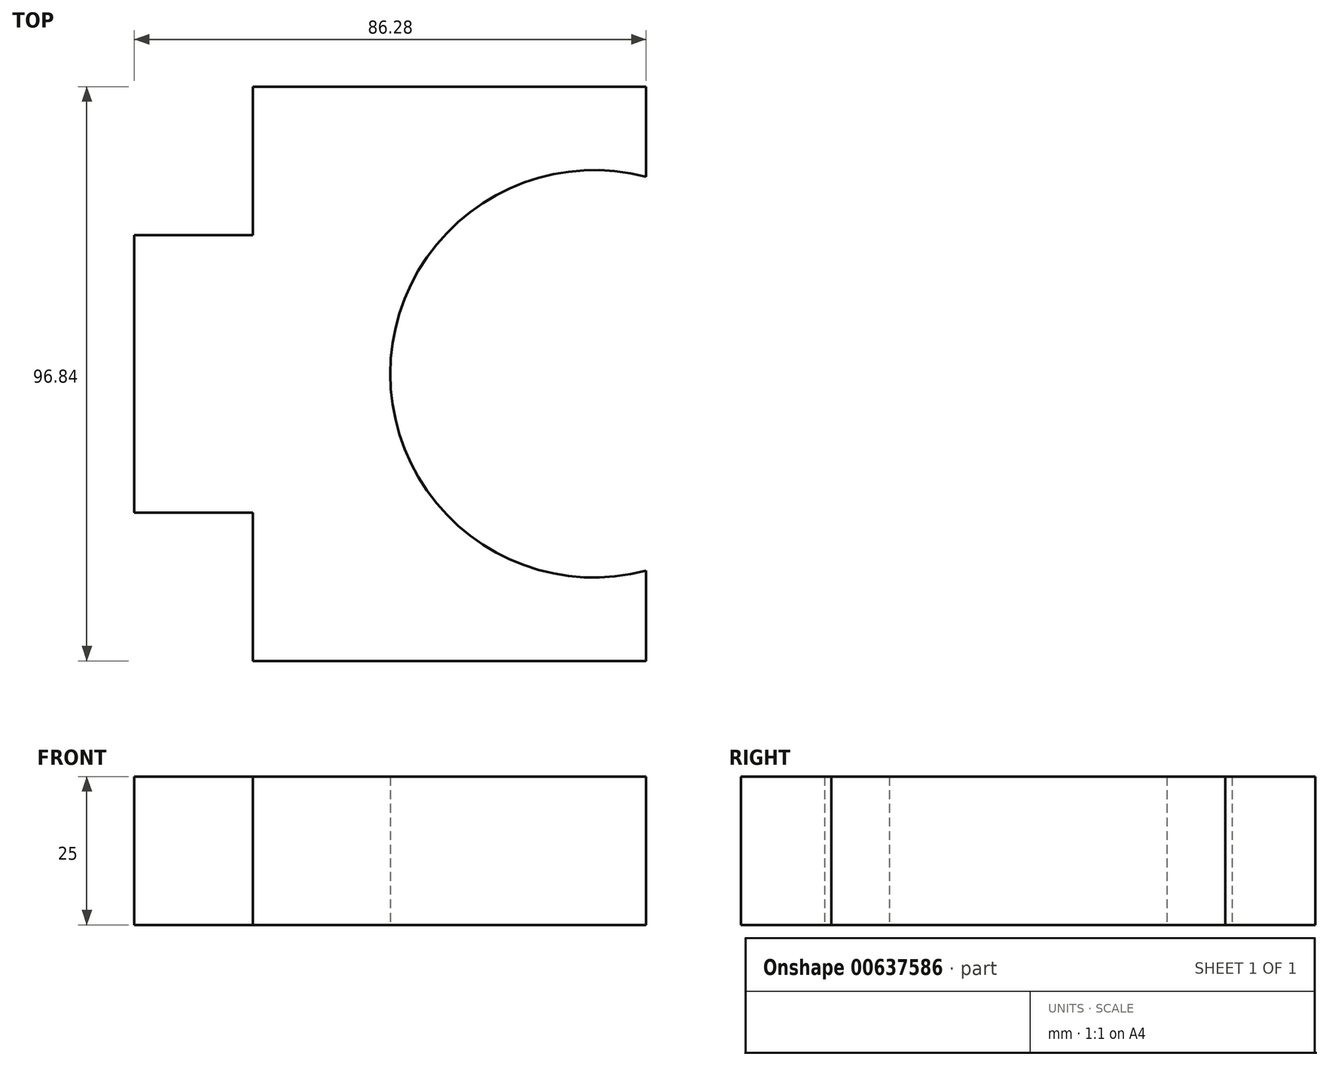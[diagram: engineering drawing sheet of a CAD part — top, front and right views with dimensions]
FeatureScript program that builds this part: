
annotation { "Feature Type Name" : "Feature", "Feature Type Description" : "" }
export const myFeature = defineFeature(function(context is Context, id is Id, definition is map)
    precondition{}
    {
        {
            var Q0;
            Q0=qCreatedBy(makeId("Top.planeOp"),FACE);
            var sketch = newSketch(context, id + "F0", { "sketchPlane" : qUnion([Q0])});
            skLineSegment(sketch, "E0", {"start": v(32.1, 48.42) * mm, "end": v(32.1, 33.2) * mm});
            skArc(sketch, "E1", {"start": v(32.1, 33.2) * mm, "mid": v(-11.04, 0) * mm, "end": v(32.1, -33.2) * mm});
            skLineSegment(sketch, "E2.trimOffspring", {"start": v(32.1, -33.2) * mm, "end": v(32.1, -48.42) * mm});
            skLineSegment(sketch, "E3", {"start": v(32.1, 48.42) * mm, "end": v(-34.2, 48.42) * mm});
            skPoint(sketch, "E4.end.orphan", {"position": v(-34.2, 21.15) * mm});
            skPoint(sketch, "E5.start.orphan", {"position": v(-34.2, -52.39) * mm});
            skLineSegment(sketch, "E6", {"start": v(32.1, -48.42) * mm, "end": v(-34.2, -48.42) * mm});
            skLineSegment(sketch, "E7", {"start": v(-34.2, -48.42) * mm, "end": v(-34.2, -23.42) * mm});
            skLineSegment(sketch, "E8", {"start": v(-34.2, 48.42) * mm, "end": v(-34.2, 23.42) * mm});
            skLineSegment(sketch, "E9", {"start": v(-34.2, 23.42) * mm, "end": v(-54.2, 23.42) * mm});
            skLineSegment(sketch, "E10", {"start": v(-34.2, -23.42) * mm, "end": v(-54.2, -23.42) * mm});
            skLineSegment(sketch, "E11", {"start": v(-54.2, 23.42) * mm, "end": v(-54.2, -23.42) * mm});
            skSolve(sketch);
        }
        {
            var Q0;
            Q0 = qSketchRegion(id + "F0", true);
            extrude(context, id + "F1", {"entities" : qUnion([Q0]), "depth" : 25 * mm, "offsetDistance" : 25 * mm});
        }
    });
